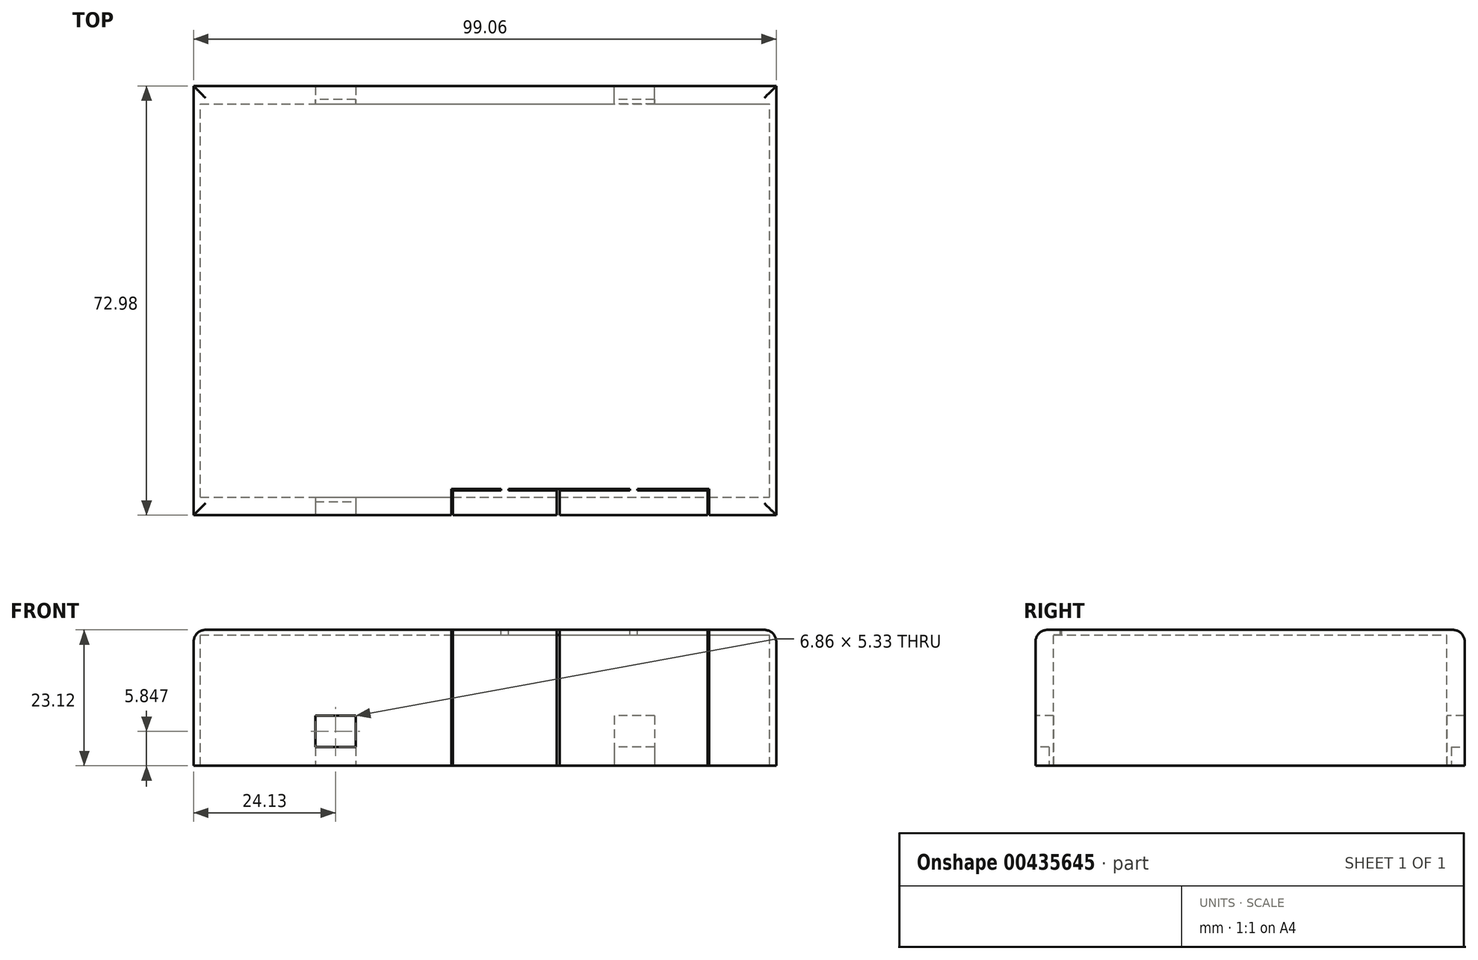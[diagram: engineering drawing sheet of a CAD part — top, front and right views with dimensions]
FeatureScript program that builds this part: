
annotation { "Feature Type Name" : "Feature", "Feature Type Description" : "" }
export const myFeature = defineFeature(function(context is Context, id is Id, definition is map)
    precondition{}
    {
        {
            var Q0;
            Q0=qCreatedBy(makeId("Top.planeOp"),FACE);
            var sketch = newSketch(context, id + "F0", { "sketchPlane" : qUnion([Q0])});
            skLineSegment(sketch, "E0.bottom", {"start": v(-49.53, 36.49) * mm, "end": v(49.53, 36.49) * mm});
            skLineSegment(sketch, "E0.top", {"start": v(-49.53, -36.49) * mm, "end": v(49.53, -36.49) * mm});
            skLineSegment(sketch, "E0.left", {"start": v(-49.53, 36.49) * mm, "end": v(-49.53, -36.49) * mm});
            skLineSegment(sketch, "E0.right", {"start": v(49.53, 36.49) * mm, "end": v(49.53, -36.49) * mm});
            skLineSegment(sketch, "E1", {"start": v(-49.53, 36.49) * mm, "end": v(49.53, -36.49) * mm, "construction": true});
            skLineSegment(sketch, "E2", {"start": v(-49.53, -36.49) * mm, "end": v(49.53, 36.49) * mm, "construction": true});
            skSolve(sketch);
        }
        {
            var Q0;
            Q0=makeQuery(id+"F0.imprint","IMPRINT",FACE,{"disambiguationData":[TD([[makeQuery(id+"F0.imprint","IMPRINT",EDGE,{"derivedFrom":sQuery(id+"F0.wireOp",EDGE,"E0.bottom")}),-1.0]])]});
            extrude(context, id + "F1", {"entities" : qUnion([Q0]), "depth" : 0.89 * mm});
        }
        {
            var Q0;
            Q0=makeQuery(id+"F1.opExtrude","CAP_FACE",FACE,{"disambiguationData":[OSD([sQuery(id+"F0.wireOp",EDGE,"E0.bottom"),sQuery(id+"F0.wireOp",EDGE,"E0.top"),sQuery(id+"F0.wireOp",EDGE,"E0.left"),sQuery(id+"F0.wireOp",EDGE,"E0.right")])],"isStart":true});
            var sketch = newSketch(context, id + "F2", { "sketchPlane" : qUnion([Q0])});
            skLineSegment(sketch, "E3.bottom", {"start": v(-49.53, -36.49) * mm, "end": v(49.53, -36.49) * mm});
            skLineSegment(sketch, "E3.top", {"start": v(-49.53, 36.49) * mm, "end": v(49.53, 36.49) * mm});
            skLineSegment(sketch, "E3.left", {"start": v(-49.53, -36.49) * mm, "end": v(-49.53, 36.49) * mm});
            skLineSegment(sketch, "E3.right", {"start": v(49.53, -36.49) * mm, "end": v(49.53, 36.49) * mm});
            skLineSegment(sketch, "E4.0", {"start": v(-48.39, 33.41) * mm, "end": v(48.39, 33.41) * mm});
            skLineSegment(sketch, "E4.2", {"start": v(-48.39, -33.41) * mm, "end": v(48.39, -33.41) * mm});
            skLineSegment(sketch, "E5", {"start": v(-48.39, 33.41) * mm, "end": v(-48.39, -33.41) * mm});
            skLineSegment(sketch, "E6", {"start": v(48.39, 33.41) * mm, "end": v(48.39, -33.41) * mm});
            skSolve(sketch);
        }
        {
            var Q0;
            Q0 = qSketchRegion(id + "F2", true);
            extrude(context, id + "F3", {"entities" : qUnion([Q0]), "operationType" : NewBodyOperationType.ADD, "depth" : 22.22 * mm});
        }
        {
            var Q0;
            Q0=makeQuery(id+"F1.opExtrude","CAP_EDGE",EDGE,{"disambiguationData":[OSD([sQuery(id+"F0.wireOp",EDGE,"E0.top")])],"isStart":false});
            var Q1;
            Q1=makeQuery(id+"F1.opExtrude","CAP_EDGE",EDGE,{"disambiguationData":[OSD([sQuery(id+"F0.wireOp",EDGE,"E0.right")])],"isStart":false});
            var Q2;
            Q2=makeQuery(id+"F1.opExtrude","CAP_EDGE",EDGE,{"disambiguationData":[OSD([sQuery(id+"F0.wireOp",EDGE,"E0.bottom")])],"isStart":false});
            var Q3;
            Q3=makeQuery(id+"F1.opExtrude","CAP_EDGE",EDGE,{"disambiguationData":[OSD([sQuery(id+"F0.wireOp",EDGE,"E0.left")])],"isStart":false});
            fillet(context, id + "F4", {"entities" : qUnion([Q0, Q1, Q2, Q3]), "radius" : 2.03 * mm, "tangentPropagation" : true, "allowEdgeOverflow" : false});
        }
        {
            var Q0;
            Q0=makeQuery(id+"F1.opExtrude","CAP_FACE",FACE,{"disambiguationData":[OSD([sQuery(id+"F0.wireOp",EDGE,"E0.bottom"),sQuery(id+"F0.wireOp",EDGE,"E0.top"),sQuery(id+"F0.wireOp",EDGE,"E0.left"),sQuery(id+"F0.wireOp",EDGE,"E0.right")])],"isStart":false});
            var sketch = newSketch(context, id + "F5", { "sketchPlane" : qUnion([Q0])});
            skLineSegment(sketch, "E7", {"start": v(12.45, -36.49) * mm, "end": v(38.1, -36.49) * mm, "construction": true});
            skLineSegment(sketch, "E8", {"start": v(25.27, -36.49) * mm, "end": v(25.27, -32.04) * mm, "construction": true});
            skLineSegment(sketch, "E9", {"start": v(12.45, -32.04) * mm, "end": v(12.45, -36.49) * mm});
            skLineSegment(sketch, "E10", {"start": v(38.1, -32.04) * mm, "end": v(38.1, -36.49) * mm});
            skLineSegment(sketch, "E11", {"start": v(12.7, -36.49) * mm, "end": v(12.7, -32.3) * mm});
            skLineSegment(sketch, "E12", {"start": v(12.7, -32.3) * mm, "end": v(24.64, -32.3) * mm});
            skLineSegment(sketch, "E13", {"start": v(24.64, -32.3) * mm, "end": v(24.64, -32.04) * mm});
            skLineSegment(sketch, "E14", {"start": v(25.9, -32.04) * mm, "end": v(25.9, -32.3) * mm});
            skLineSegment(sketch, "E15", {"start": v(25.9, -32.3) * mm, "end": v(37.85, -32.3) * mm});
            skLineSegment(sketch, "E16", {"start": v(37.85, -32.3) * mm, "end": v(37.85, -36.49) * mm});
            skLineSegment(sketch, "E17", {"start": v(12.45, -32.04) * mm, "end": v(24.64, -32.04) * mm});
            skLineSegment(sketch, "E18", {"start": v(25.9, -32.04) * mm, "end": v(38.1, -32.04) * mm});
            skLineSegment(sketch, "E19", {"start": v(24.64, -32.04) * mm, "end": v(25.9, -32.04) * mm, "construction": true});
            skLineSegment(sketch, "E20", {"start": v(12.45, -36.49) * mm, "end": v(12.7, -36.49) * mm});
            skLineSegment(sketch, "E21", {"start": v(37.85, -36.49) * mm, "end": v(38.1, -36.49) * mm});
            skSolve(sketch);
        }
        {
            var Q0;
            Q0 = qSketchRegion(id + "F5", true);
            extrude(context, id + "F6", {"entities" : qUnion([Q0]), "operationType" : NewBodyOperationType.REMOVE, "oppositeDirection" : true, "depth" : 25.4 * mm});
        }
        {
            var Q0;
            Q0=makeQuery(id+"F1.opExtrude","CAP_FACE",FACE,{"disambiguationData":[OSD([sQuery(id+"F0.wireOp",EDGE,"E0.bottom"),sQuery(id+"F0.wireOp",EDGE,"E0.top"),sQuery(id+"F0.wireOp",EDGE,"E0.left"),sQuery(id+"F0.wireOp",EDGE,"E0.right")])],"isStart":false});
            var sketch = newSketch(context, id + "F7", { "sketchPlane" : qUnion([Q0])});
            skLineSegment(sketch, "E22", {"start": v(4, -32.04) * mm, "end": v(12.45, -32.04) * mm});
            skLineSegment(sketch, "E23", {"start": v(12.45, -32.04) * mm, "end": v(12.45, -36.49) * mm});
            skLineSegment(sketch, "E24", {"start": v(12.45, -36.49) * mm, "end": v(12.2, -36.49) * mm});
            skLineSegment(sketch, "E25", {"start": v(12.2, -36.49) * mm, "end": v(12.2, -32.3) * mm});
            skLineSegment(sketch, "E26", {"start": v(12.2, -32.3) * mm, "end": v(4, -32.3) * mm});
            skLineSegment(sketch, "E27", {"start": v(4, -32.3) * mm, "end": v(4, -32.04) * mm});
            skLineSegment(sketch, "E28", {"start": v(4, -32.04) * mm, "end": v(2.73, -32.04) * mm, "construction": true});
            skLineSegment(sketch, "E29", {"start": v(2.73, -32.04) * mm, "end": v(-5.71, -32.04) * mm});
            skLineSegment(sketch, "E30", {"start": v(-5.71, -32.04) * mm, "end": v(-5.71, -36.49) * mm});
            skLineSegment(sketch, "E31", {"start": v(-5.71, -36.49) * mm, "end": v(-5.46, -36.49) * mm});
            skLineSegment(sketch, "E32", {"start": v(-5.46, -36.49) * mm, "end": v(-5.46, -32.3) * mm});
            skLineSegment(sketch, "E33", {"start": v(-5.46, -32.3) * mm, "end": v(2.73, -32.3) * mm});
            skLineSegment(sketch, "E34", {"start": v(2.73, -32.3) * mm, "end": v(2.73, -32.04) * mm});
            skLineSegment(sketch, "E35", {"start": v(-5.46, -36.49) * mm, "end": v(12.2, -36.49) * mm, "construction": true});
            skLineSegment(sketch, "E36", {"start": v(3.37, -32.04) * mm, "end": v(3.37, -36.49) * mm, "construction": true});
            skSolve(sketch);
        }
        {
            var Q0;
            Q0 = qSketchRegion(id + "F7", true);
            extrude(context, id + "F8", {"entities" : qUnion([Q0]), "operationType" : NewBodyOperationType.REMOVE, "oppositeDirection" : true, "depth" : 25.4 * mm});
        }
        {
            var Q0;
            Q0=qCreatedBy(makeId("Right.planeOp"),FACE);
            cPlane(context, id + "F9", {"entities" : qUnion([Q0]), "cplaneType" : CPlaneType.OFFSET, "offset" : 25.4 * mm, "oppositeDirection" : true, "width" : 152.4 * mm, "height" : 152.4 * mm});
        }
        {
            var Q0;
            {var subQ0=sQuery(id+"F0.wireOp",EDGE,"E0.top");var subQ4=sQuery(id+"F2.wireOp",EDGE,"E3.top");var subQ6=sQuery(id+"F0.wireOp",EDGE,"E0.left");var subQ7=makeQuery(id+"F1.opExtrude","SWEPT_FACE",FACE,{"disambiguationData":[OSD([subQ6])]});Q0=makeQuery(id+"F8.boolean.opBoolean","SPLIT",FACE,{"disambiguationData":[TD([subQ7])],"derivedFrom":makeQuery(id+"F6.boolean.opBoolean","SPLIT",FACE,{"disambiguationData":[TD([subQ7])],"derivedFrom":makeQuery(id+"F3.boolean.opBoolean","MERGE",FACE,{"derivedFrom":[makeQuery(id+"F1.opExtrude","SWEPT_FACE",FACE,{"disambiguationData":[OSD([subQ0])]}),makeQuery(id+"F3.opExtrude","SWEPT_FACE",FACE,{"disambiguationData":[OSD([subQ4])]})]})})});}
            var sketch = newSketch(context, id + "F10", { "sketchPlane" : qUnion([Q0])});
            skLineSegment(sketch, "E37.bottom", {"start": v(-28.83, -13.72) * mm, "end": v(-21.97, -13.72) * mm});
            skLineSegment(sketch, "E37.top", {"start": v(-28.83, -19.05) * mm, "end": v(-21.97, -19.05) * mm});
            skLineSegment(sketch, "E37.left", {"start": v(-28.83, -13.72) * mm, "end": v(-28.83, -19.05) * mm});
            skLineSegment(sketch, "E37.right", {"start": v(-21.97, -13.72) * mm, "end": v(-21.97, -19.05) * mm});
            skSolve(sketch);
        }
        {
            var Q0;
            Q0 = qSketchRegion(id + "F10", true);
            extrude(context, id + "F11", {"entities" : qUnion([Q0]), "operationType" : NewBodyOperationType.REMOVE, "endBound" : BoundingType.THROUGH_ALL, "oppositeDirection" : true, "depth" : 25.4 * mm});
        }
        {
            var Q0;
            {var subQ0=sQuery(id+"F2.wireOp",EDGE,"E4.2");var subQ2=sQuery(id+"F2.wireOp",EDGE,"E4.0");var subQ4=sQuery(id+"F2.wireOp",EDGE,"E3.right");var subQ6=sQuery(id+"F2.wireOp",EDGE,"E3.bottom");var subQ9=makeQuery(id+"F1.opExtrude","SWEPT_FACE",FACE,{"disambiguationData":[OSD([sQuery(id+"F0.wireOp",EDGE,"E0.bottom")])]});var subQ10=sQuery(id+"F2.wireOp",EDGE,"E3.left");var subQ14=sQuery(id+"F2.wireOp",EDGE,"E3.top");var subQ16=sQuery(id+"F2.wireOp",EDGE,"E5");var subQ18=sQuery(id+"F2.wireOp",EDGE,"E6");Q0=makeQuery(id+"F8.boolean.opBoolean","SPLIT",FACE,{"disambiguationData":[TD([subQ9])],"derivedFrom":makeQuery(id+"F6.boolean.opBoolean","SPLIT",FACE,{"disambiguationData":[TD([subQ9])],"derivedFrom":makeQuery(id+"F3.opExtrude","CAP_FACE",FACE,{"disambiguationData":[OSD([subQ6,subQ14,subQ10,subQ4,subQ2,subQ0,subQ16,subQ18])],"isStart":false})})});}
            var sketch = newSketch(context, id + "F12", { "sketchPlane" : qUnion([Q0])});
            skLineSegment(sketch, "E38.bottom", {"start": v(-28.83, 33.41) * mm, "end": v(-21.97, 33.41) * mm});
            skLineSegment(sketch, "E38.top", {"start": v(-28.83, 34.18) * mm, "end": v(-21.97, 34.18) * mm});
            skLineSegment(sketch, "E38.left", {"start": v(-28.83, 33.41) * mm, "end": v(-28.83, 34.18) * mm});
            skLineSegment(sketch, "E38.right", {"start": v(-21.97, 33.41) * mm, "end": v(-21.97, 34.18) * mm});
            skLineSegment(sketch, "E39.MirrorCS", {"start": v(-28.83, -33.41) * mm, "end": v(-28.83, -34.18) * mm});
            skLineSegment(sketch, "E40.MirrorCS", {"start": v(-28.83, -34.18) * mm, "end": v(-21.97, -34.18) * mm});
            skLineSegment(sketch, "E41.MirrorCS", {"start": v(-28.83, -33.41) * mm, "end": v(-21.97, -33.41) * mm});
            skLineSegment(sketch, "E42.MirrorCS", {"start": v(-21.97, -33.41) * mm, "end": v(-21.97, -34.18) * mm});
            skSolve(sketch);
        }
        {
            var Q0;
            Q0 = qSketchRegion(id + "F12", true);
            extrude(context, id + "F13", {"entities" : qUnion([Q0]), "operationType" : NewBodyOperationType.REMOVE, "endBound" : BoundingType.UP_TO_NEXT, "oppositeDirection" : true, "depth" : 25.4 * mm});
        }
        {
            var Q0;
            Q0=qCreatedBy(makeId("Right.planeOp"),FACE);
            cPlane(context, id + "F14", {"entities" : qUnion([Q0]), "cplaneType" : CPlaneType.OFFSET, "offset" : 25.4 * mm, "width" : 152.4 * mm, "height" : 152.4 * mm});
        }
        {
            var Q0;
            Q0=makeQuery(id+"F3.boolean.opBoolean","MERGE",FACE,{"derivedFrom":[makeQuery(id+"F1.opExtrude","SWEPT_FACE",FACE,{"disambiguationData":[OSD([sQuery(id+"F0.wireOp",EDGE,"E0.bottom")])]}),makeQuery(id+"F3.opExtrude","SWEPT_FACE",FACE,{"disambiguationData":[OSD([sQuery(id+"F2.wireOp",EDGE,"E3.bottom")])]})]});
            var sketch = newSketch(context, id + "F15", { "sketchPlane" : qUnion([Q0])});
            skLineSegment(sketch, "E43.bottom", {"start": v(-28.83, -13.72) * mm, "end": v(-21.97, -13.72) * mm});
            skLineSegment(sketch, "E43.top", {"start": v(-28.83, -19.05) * mm, "end": v(-21.97, -19.05) * mm});
            skLineSegment(sketch, "E43.left", {"start": v(-28.83, -13.72) * mm, "end": v(-28.83, -19.05) * mm});
            skLineSegment(sketch, "E43.right", {"start": v(-21.97, -13.72) * mm, "end": v(-21.97, -19.05) * mm});
            skSolve(sketch);
        }
        {
            var Q0;
            Q0 = qSketchRegion(id + "F15", true);
            extrude(context, id + "F16", {"entities" : qUnion([Q0]), "operationType" : NewBodyOperationType.REMOVE, "endBound" : BoundingType.UP_TO_NEXT, "oppositeDirection" : true, "depth" : 25.4 * mm});
        }
        {
            var Q0;
            {var subQ0=sQuery(id+"F2.wireOp",EDGE,"E4.2");var subQ2=sQuery(id+"F2.wireOp",EDGE,"E4.0");var subQ4=sQuery(id+"F2.wireOp",EDGE,"E3.right");var subQ6=sQuery(id+"F2.wireOp",EDGE,"E3.bottom");var subQ9=makeQuery(id+"F1.opExtrude","SWEPT_FACE",FACE,{"disambiguationData":[OSD([sQuery(id+"F0.wireOp",EDGE,"E0.bottom")])]});var subQ10=sQuery(id+"F2.wireOp",EDGE,"E3.left");var subQ14=sQuery(id+"F2.wireOp",EDGE,"E3.top");var subQ16=sQuery(id+"F2.wireOp",EDGE,"E5");var subQ18=sQuery(id+"F2.wireOp",EDGE,"E6");Q0=makeQuery(id+"F8.boolean.opBoolean","SPLIT",FACE,{"disambiguationData":[TD([subQ9])],"derivedFrom":makeQuery(id+"F6.boolean.opBoolean","SPLIT",FACE,{"disambiguationData":[TD([subQ9])],"derivedFrom":makeQuery(id+"F3.opExtrude","CAP_FACE",FACE,{"disambiguationData":[OSD([subQ6,subQ14,subQ10,subQ4,subQ2,subQ0,subQ16,subQ18])],"isStart":false})})});}
            var sketch = newSketch(context, id + "F17", { "sketchPlane" : qUnion([Q0])});
            skLineSegment(sketch, "E44", {"start": v(21.97, -33.41) * mm, "end": v(21.97, -34.18) * mm});
            skLineSegment(sketch, "E45", {"start": v(21.97, -34.18) * mm, "end": v(28.83, -34.18) * mm});
            skLineSegment(sketch, "E46", {"start": v(28.83, -34.18) * mm, "end": v(28.83, -33.41) * mm});
            skLineSegment(sketch, "E47", {"start": v(28.83, -33.41) * mm, "end": v(21.97, -33.41) * mm});
            skSolve(sketch);
        }
        {
            var Q0;
            Q0 = qSketchRegion(id + "F17", true);
            extrude(context, id + "F18", {"entities" : qUnion([Q0]), "operationType" : NewBodyOperationType.REMOVE, "endBound" : BoundingType.UP_TO_NEXT, "oppositeDirection" : true, "depth" : 25.4 * mm});
        }
    });
